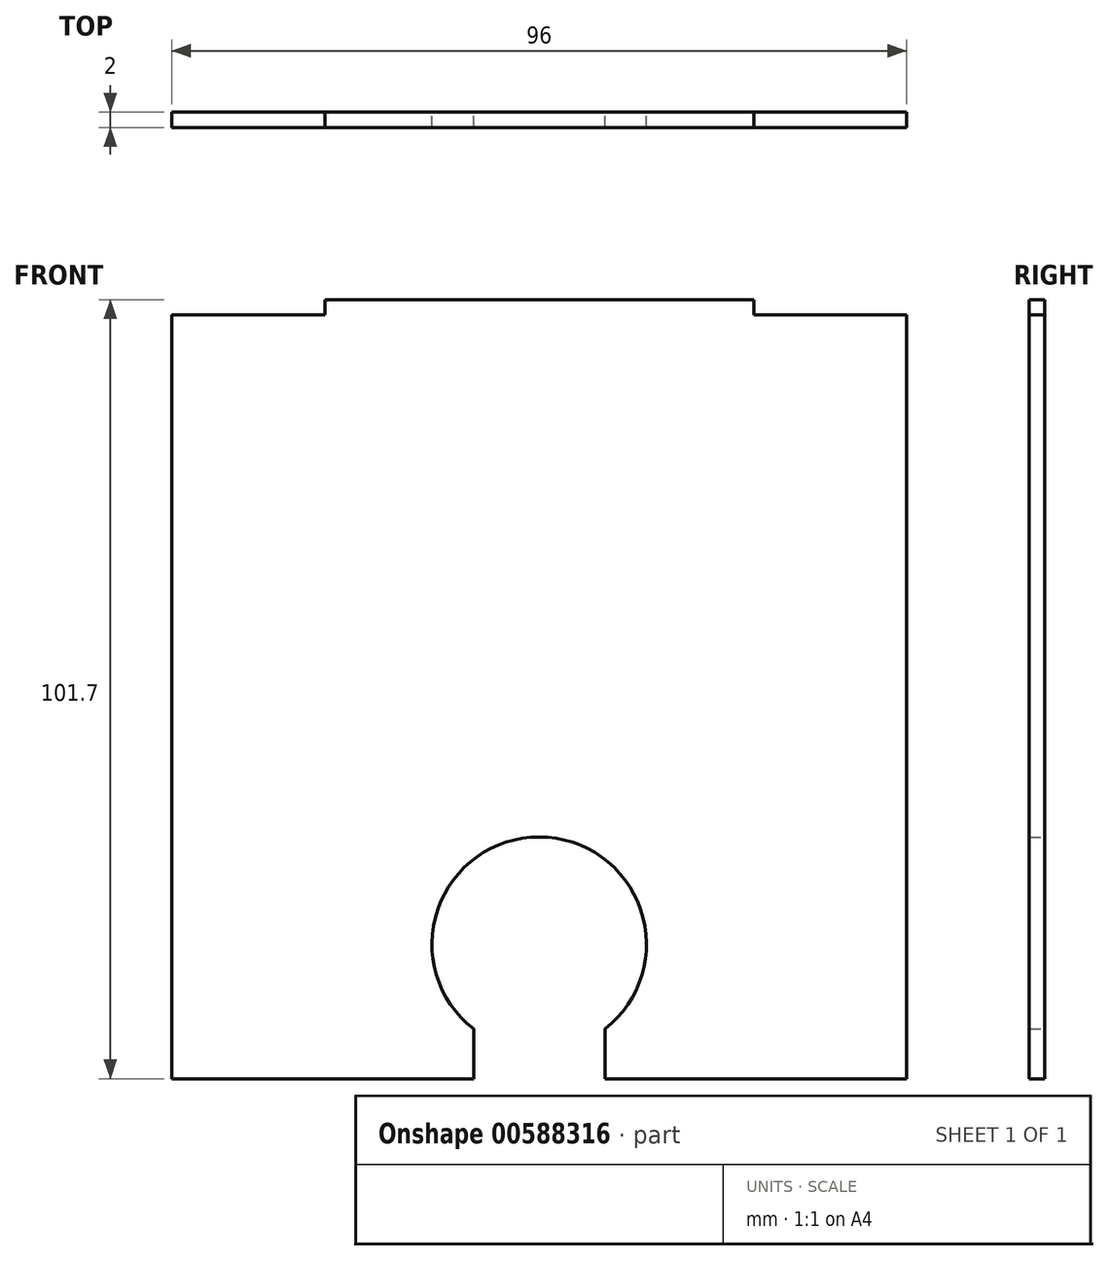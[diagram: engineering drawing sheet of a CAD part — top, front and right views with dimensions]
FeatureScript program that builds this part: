
annotation { "Feature Type Name" : "Feature", "Feature Type Description" : "" }
export const myFeature = defineFeature(function(context is Context, id is Id, definition is map)
    precondition{}
    {
        {
            var Q0;
            Q0=qCreatedBy(makeId("Front.planeOp"),FACE);
            var sketch = newSketch(context, id + "F0", { "sketchPlane" : qUnion([Q0])});
            skLineSegment(sketch, "E0.bottom", {"start": v(-14.53, 56.72) * mm, "end": v(5.47, 56.72) * mm});
            skLineSegment(sketch, "E0.top", {"start": v(-14.53, -42.98) * mm, "end": v(24.9, -42.98) * mm});
            skLineSegment(sketch, "E0.left", {"start": v(-14.53, 56.72) * mm, "end": v(-14.53, -42.98) * mm});
            skLineSegment(sketch, "E0.right", {"start": v(81.47, 56.72) * mm, "end": v(81.47, -42.98) * mm});
            skLineSegment(sketch, "E1", {"start": v(5.47, 56.72) * mm, "end": v(5.47, 58.72) * mm});
            skLineSegment(sketch, "E2", {"start": v(81.47, 56.72) * mm, "end": v(61.47, 56.72) * mm});
            skLineSegment(sketch, "E3", {"start": v(61.47, 56.72) * mm, "end": v(61.47, 58.72) * mm});
            skLineSegment(sketch, "E4", {"start": v(61.47, 58.72) * mm, "end": v(5.47, 58.72) * mm});
            skLineSegment(sketch, "E5.trimOffspring", {"start": v(61.47, 56.72) * mm, "end": v(81.47, 56.72) * mm});
            skArc(sketch, "E6", {"start": v(42.04, -36.5) * mm, "mid": v(33.47, -11.42) * mm, "end": v(24.9, -36.5) * mm});
            skLineSegment(sketch, "E7", {"start": v(42.04, -42.98) * mm, "end": v(42.04, -36.5) * mm});
            skLineSegment(sketch, "E8", {"start": v(24.9, -42.98) * mm, "end": v(24.9, -36.5) * mm});
            skPoint(sketch, "E9.start.orphan", {"position": v(33.47, -42.98) * mm});
            skLineSegment(sketch, "E10.trimOffspring", {"start": v(42.04, -42.98) * mm, "end": v(81.47, -42.98) * mm});
            skSolve(sketch);
        }
        {
            var Q0;
            Q0=makeQuery(id+"F0.imprint","IMPRINT",FACE,{"disambiguationData":[TD([[makeQuery(id+"F0.imprint","IMPRINT",EDGE,{"derivedFrom":sQuery(id+"F0.wireOp",EDGE,"E0.top")}),1.0]])]});
            extrude(context, id + "F1", {"entities" : qUnion([Q0]), "depth" : 2 * mm, "offsetDistance" : 25 * mm});
        }
    });
